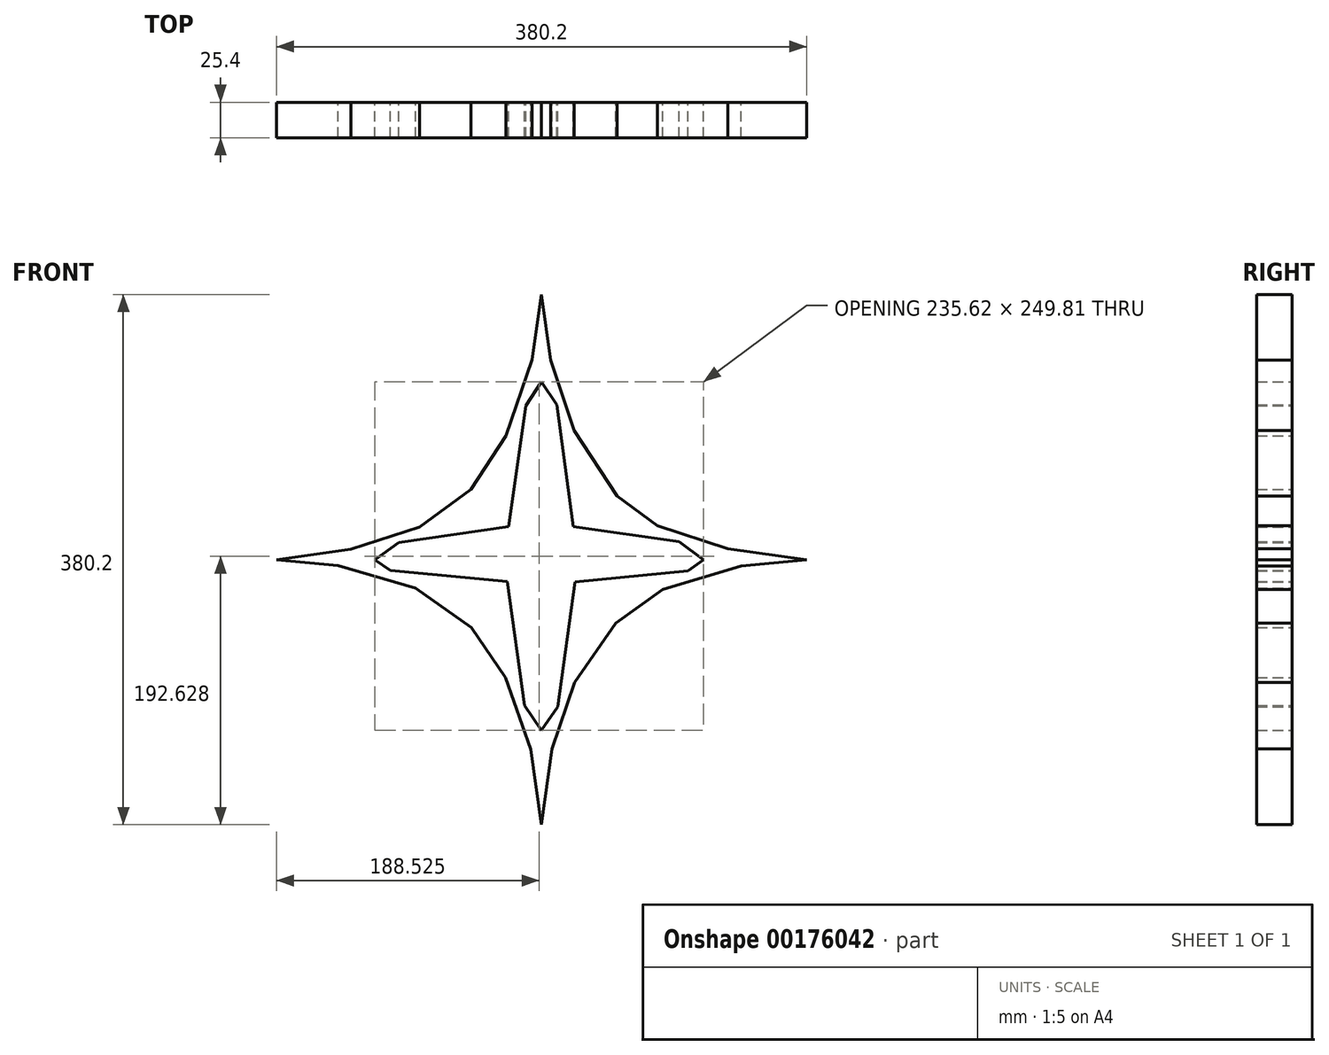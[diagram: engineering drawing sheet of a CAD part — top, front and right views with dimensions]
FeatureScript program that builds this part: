
annotation { "Feature Type Name" : "Feature", "Feature Type Description" : "" }
export const myFeature = defineFeature(function(context is Context, id is Id, definition is map)
    precondition{}
    {
        {
            var Q0;
            Q0=qCreatedBy(makeId("Front.planeOp"),FACE);
            var sketch = newSketch(context, id + "F0", { "sketchPlane" : qUnion([Q0])});
            skPoint(sketch, "E0", {"position": v(-190.1, 0) * mm});
            skPoint(sketch, "E1", {"position": v(0, 190.1) * mm});
            skPoint(sketch, "E2", {"position": v(190.1, 0) * mm});
            skPoint(sketch, "E3", {"position": v(0, -190.1) * mm});
            skPoint(sketch, "E4", {"position": v(-160.1, 0) * mm});
            skPoint(sketch, "E5", {"position": v(-119.39, 0) * mm});
            skPoint(sketch, "E6", {"position": v(-83.61, 0) * mm});
            skPoint(sketch, "E7", {"position": v(-55.85, 0) * mm});
            skPoint(sketch, "E8", {"position": v(-26.86, 0) * mm});
            skPoint(sketch, "E9", {"position": v(26.18, 0) * mm});
            skPoint(sketch, "E10", {"position": v(84.78, 0) * mm});
            skPoint(sketch, "E11", {"position": v(116.24, 0) * mm});
            skPoint(sketch, "E12", {"position": v(158.18, 0) * mm});
            skPoint(sketch, "E13", {"position": v(0, -18.14) * mm});
            skPoint(sketch, "E14", {"position": v(53.94, 0) * mm});
            skPoint(sketch, "E15", {"position": v(0, -47.13) * mm});
            skPoint(sketch, "E16", {"position": v(0, -84.13) * mm});
            skPoint(sketch, "E17", {"position": v(0, -122.38) * mm});
            skPoint(sketch, "E18", {"position": v(0, -157.54) * mm});
            skPoint(sketch, "E19", {"position": v(0, 26.9) * mm});
            skPoint(sketch, "E20", {"position": v(0, 51.56) * mm});
            skPoint(sketch, "E21", {"position": v(0, 87.34) * mm});
            skPoint(sketch, "E22", {"position": v(0, 127.43) * mm});
            skPoint(sketch, "E23", {"position": v(0, 162.6) * mm});
            skLineSegment(sketch, "E24", {"start": v(0, 190.1) * mm, "end": v(-26.86, 0) * mm});
            skLineSegment(sketch, "E25", {"start": v(0, 162.6) * mm, "end": v(-55.85, 0) * mm});
            skLineSegment(sketch, "E26", {"start": v(0, 127.43) * mm, "end": v(-83.61, 0) * mm});
            skLineSegment(sketch, "E27", {"start": v(0, 87.34) * mm, "end": v(-119.39, 0) * mm});
            skLineSegment(sketch, "E28", {"start": v(0, 51.56) * mm, "end": v(-160.1, 0) * mm});
            skLineSegment(sketch, "E29", {"start": v(0, 26.9) * mm, "end": v(-190.1, 0) * mm});
            skLineSegment(sketch, "E30", {"start": v(-190.1, 0) * mm, "end": v(0, -18.14) * mm});
            skLineSegment(sketch, "E31", {"start": v(-160.1, 0) * mm, "end": v(0, -47.13) * mm});
            skLineSegment(sketch, "E32", {"start": v(-119.39, 0) * mm, "end": v(0, -84.13) * mm});
            skLineSegment(sketch, "E33", {"start": v(-83.61, 0) * mm, "end": v(0, -122.38) * mm});
            skLineSegment(sketch, "E34", {"start": v(-55.85, 0) * mm, "end": v(0, -157.54) * mm});
            skLineSegment(sketch, "E35", {"start": v(-26.86, 0) * mm, "end": v(0, -190.1) * mm});
            skLineSegment(sketch, "E36", {"start": v(0, 190.1) * mm, "end": v(26.18, 0) * mm});
            skLineSegment(sketch, "E37", {"start": v(0, 162.6) * mm, "end": v(53.94, 0) * mm});
            skLineSegment(sketch, "E38", {"start": v(0, 127.43) * mm, "end": v(84.78, 0) * mm});
            skLineSegment(sketch, "E39", {"start": v(-1.32, 86.87) * mm, "end": v(116.24, 0) * mm});
            skLineSegment(sketch, "E40", {"start": v(0, 51.56) * mm, "end": v(158.18, 0) * mm});
            skLineSegment(sketch, "E41", {"start": v(0, 26.9) * mm, "end": v(190.1, 0) * mm});
            skLineSegment(sketch, "E42", {"start": v(0, -18.14) * mm, "end": v(190.1, 0) * mm});
            skLineSegment(sketch, "E43", {"start": v(0, -47.13) * mm, "end": v(158.18, 0) * mm});
            skLineSegment(sketch, "E44", {"start": v(0, -84.13) * mm, "end": v(116.24, 0) * mm});
            skLineSegment(sketch, "E45", {"start": v(0, -122.38) * mm, "end": v(84.78, 0) * mm});
            skLineSegment(sketch, "E46", {"start": v(0, -157.54) * mm, "end": v(53.94, 0) * mm});
            skLineSegment(sketch, "E47", {"start": v(0, -190.1) * mm, "end": v(26.18, 0) * mm});
            skSolve(sketch);
        }
        {
            var Q0;
            Q0 = qSketchRegion(id + "F0", true);
            var Q1;
            {var subQ0=sQuery(id+"F0.wireOp",EDGE,"E28");var subQ1=sQuery(id+"F0.wireOp",EDGE,"E24");var subQ2=makeQuery(id+"F0.imprint","INTERSECT",VERTEX,{"derivedFrom":[subQ1,subQ0]});Q1=makeQuery(id+"F0.imprint","IMPRINT",FACE,{"disambiguationData":[TD([[makeQuery(id+"F0.imprint","IMPRINT",EDGE,{"disambiguationData":[TD([[subQ2,-1.0]])],"derivedFrom":subQ1}),-1.0]])]});}
            var Q2;
            {var subQ0=sQuery(id+"F0.wireOp",EDGE,"E28");var subQ1=sQuery(id+"F0.wireOp",EDGE,"E25");var subQ2=makeQuery(id+"F0.imprint","INTERSECT",VERTEX,{"derivedFrom":[subQ1,subQ0]});Q2=makeQuery(id+"F0.imprint","IMPRINT",FACE,{"disambiguationData":[TD([[makeQuery(id+"F0.imprint","IMPRINT",EDGE,{"disambiguationData":[TD([[subQ2,-1.0]])],"derivedFrom":subQ1}),-1.0]])]});}
            var Q3;
            {var subQ0=sQuery(id+"F0.wireOp",EDGE,"E27");var subQ1=sQuery(id+"F0.wireOp",EDGE,"E24");var subQ2=makeQuery(id+"F0.imprint","INTERSECT",VERTEX,{"derivedFrom":[subQ1,subQ0]});Q3=makeQuery(id+"F0.imprint","IMPRINT",FACE,{"disambiguationData":[TD([[makeQuery(id+"F0.imprint","IMPRINT",EDGE,{"disambiguationData":[TD([[subQ2,-1.0]])],"derivedFrom":subQ1}),-1.0]])]});}
            var Q4;
            {var subQ0=sQuery(id+"F0.wireOp",EDGE,"E33");var subQ1=sQuery(id+"F0.wireOp",EDGE,"E30");var subQ2=makeQuery(id+"F0.imprint","INTERSECT",VERTEX,{"derivedFrom":[subQ1,subQ0]});Q4=makeQuery(id+"F0.imprint","IMPRINT",FACE,{"disambiguationData":[TD([[makeQuery(id+"F0.imprint","IMPRINT",EDGE,{"disambiguationData":[TD([[subQ2,-1.0]])],"derivedFrom":subQ1}),-1.0]])]});}
            var Q5;
            {var subQ0=sQuery(id+"F0.wireOp",EDGE,"E34");var subQ1=sQuery(id+"F0.wireOp",EDGE,"E30");var subQ2=makeQuery(id+"F0.imprint","INTERSECT",VERTEX,{"derivedFrom":[subQ1,subQ0]});Q5=makeQuery(id+"F0.imprint","IMPRINT",FACE,{"disambiguationData":[TD([[makeQuery(id+"F0.imprint","IMPRINT",EDGE,{"disambiguationData":[TD([[subQ2,-1.0]])],"derivedFrom":subQ1}),-1.0]])]});}
            var Q6;
            {var subQ0=sQuery(id+"F0.wireOp",EDGE,"E34");var subQ1=sQuery(id+"F0.wireOp",EDGE,"E31");var subQ2=makeQuery(id+"F0.imprint","INTERSECT",VERTEX,{"derivedFrom":[subQ1,subQ0]});Q6=makeQuery(id+"F0.imprint","IMPRINT",FACE,{"disambiguationData":[TD([[makeQuery(id+"F0.imprint","IMPRINT",EDGE,{"disambiguationData":[TD([[subQ2,-1.0]])],"derivedFrom":subQ1}),-1.0]])]});}
            var Q7;
            {var subQ0=sQuery(id+"F0.wireOp",EDGE,"E47");var subQ1=sQuery(id+"F0.wireOp",EDGE,"E43");var subQ2=makeQuery(id+"F0.imprint","INTERSECT",VERTEX,{"derivedFrom":[subQ1,subQ0]});Q7=makeQuery(id+"F0.imprint","IMPRINT",FACE,{"disambiguationData":[TD([[makeQuery(id+"F0.imprint","IMPRINT",EDGE,{"disambiguationData":[TD([[subQ2,-1.0]])],"derivedFrom":subQ1}),-1.0]])]});}
            var Q8;
            {var subQ0=sQuery(id+"F0.wireOp",EDGE,"E47");var subQ1=sQuery(id+"F0.wireOp",EDGE,"E42");var subQ2=makeQuery(id+"F0.imprint","INTERSECT",VERTEX,{"derivedFrom":[subQ1,subQ0]});Q8=makeQuery(id+"F0.imprint","IMPRINT",FACE,{"disambiguationData":[TD([[makeQuery(id+"F0.imprint","IMPRINT",EDGE,{"disambiguationData":[TD([[subQ2,-1.0]])],"derivedFrom":subQ1}),-1.0]])]});}
            var Q9;
            {var subQ0=sQuery(id+"F0.wireOp",EDGE,"E39");var subQ1=sQuery(id+"F0.wireOp",EDGE,"E36");var subQ2=makeQuery(id+"F0.imprint","INTERSECT",VERTEX,{"derivedFrom":[subQ1,subQ0]});Q9=makeQuery(id+"F0.imprint","IMPRINT",FACE,{"disambiguationData":[TD([[makeQuery(id+"F0.imprint","IMPRINT",EDGE,{"disambiguationData":[TD([[subQ2,-1.0]])],"derivedFrom":subQ1}),1.0]])]});}
            var Q10;
            {var subQ0=sQuery(id+"F0.wireOp",EDGE,"E40");var subQ1=sQuery(id+"F0.wireOp",EDGE,"E36");var subQ2=makeQuery(id+"F0.imprint","INTERSECT",VERTEX,{"derivedFrom":[subQ1,subQ0]});Q10=makeQuery(id+"F0.imprint","IMPRINT",FACE,{"disambiguationData":[TD([[makeQuery(id+"F0.imprint","IMPRINT",EDGE,{"disambiguationData":[TD([[subQ2,-1.0]])],"derivedFrom":subQ1}),1.0]])]});}
            var Q11;
            {var subQ0=sQuery(id+"F0.wireOp",EDGE,"E40");var subQ1=sQuery(id+"F0.wireOp",EDGE,"E37");var subQ2=makeQuery(id+"F0.imprint","INTERSECT",VERTEX,{"derivedFrom":[subQ1,subQ0]});Q11=makeQuery(id+"F0.imprint","IMPRINT",FACE,{"disambiguationData":[TD([[makeQuery(id+"F0.imprint","IMPRINT",EDGE,{"disambiguationData":[TD([[subQ2,-1.0]])],"derivedFrom":subQ1}),1.0]])]});}
            var Q12;
            {var subQ0=sQuery(id+"F0.wireOp",EDGE,"E46");var subQ1=sQuery(id+"F0.wireOp",EDGE,"E42");var subQ2=makeQuery(id+"F0.imprint","INTERSECT",VERTEX,{"derivedFrom":[subQ1,subQ0]});Q12=makeQuery(id+"F0.imprint","IMPRINT",FACE,{"disambiguationData":[TD([[makeQuery(id+"F0.imprint","IMPRINT",EDGE,{"disambiguationData":[TD([[subQ2,-1.0]])],"derivedFrom":subQ1}),-1.0]])]});}
            extrude(context, id + "F1", {"entities" : qUnion([Q0, Q1, Q2, Q3, Q4, Q5, Q6, Q7, Q8, Q9, Q10, Q11, Q12]), "depth" : 25.4 * mm});
        }
    });
